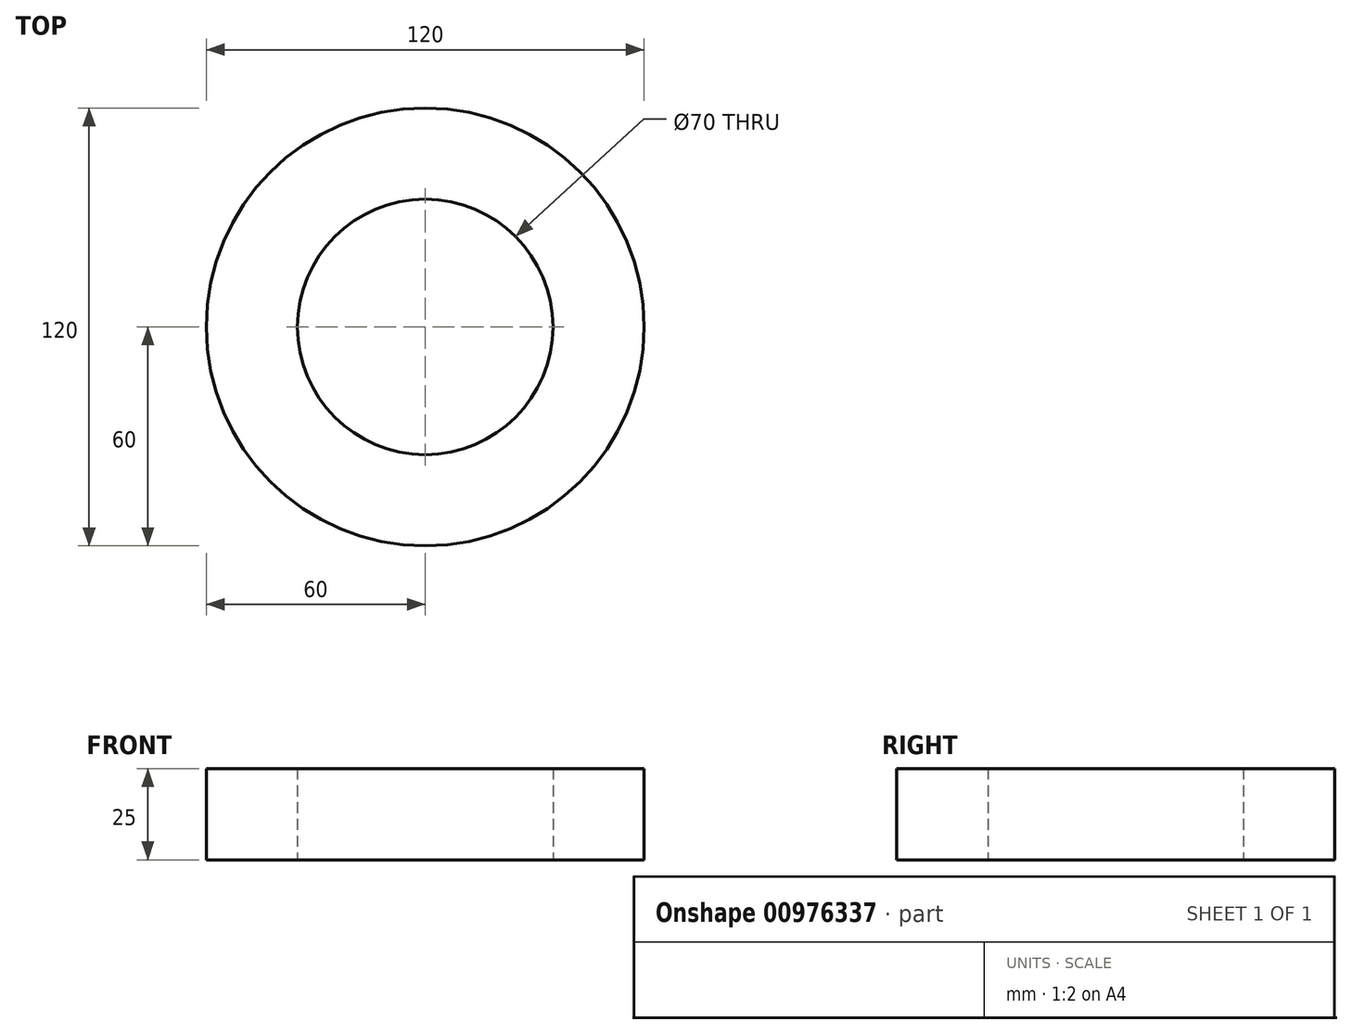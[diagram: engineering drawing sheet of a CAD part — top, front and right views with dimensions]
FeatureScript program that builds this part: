
annotation { "Feature Type Name" : "Feature", "Feature Type Description" : "" }
export const myFeature = defineFeature(function(context is Context, id is Id, definition is map)
    precondition{}
    {
        {
            var Q0;
            Q0=qCreatedBy(makeId("Top.planeOp"),FACE);
            var sketch = newSketch(context, id + "F0", { "sketchPlane" : qUnion([Q0])});
            skCircle(sketch, "E0", {"center": v(0, 0) * mm, "radius": 60 * mm});
            skCircle(sketch, "E1", {"center": v(0, 0) * mm, "radius": 35 * mm});
            skSolve(sketch);
        }
        {
            var Q0;
            Q0 = qSketchRegion(id + "F0", true);
            extrude(context, id + "F1", {"entities" : qUnion([Q0]), "depth" : 25 * mm, "offsetDistance" : 25 * mm});
        }
    });
